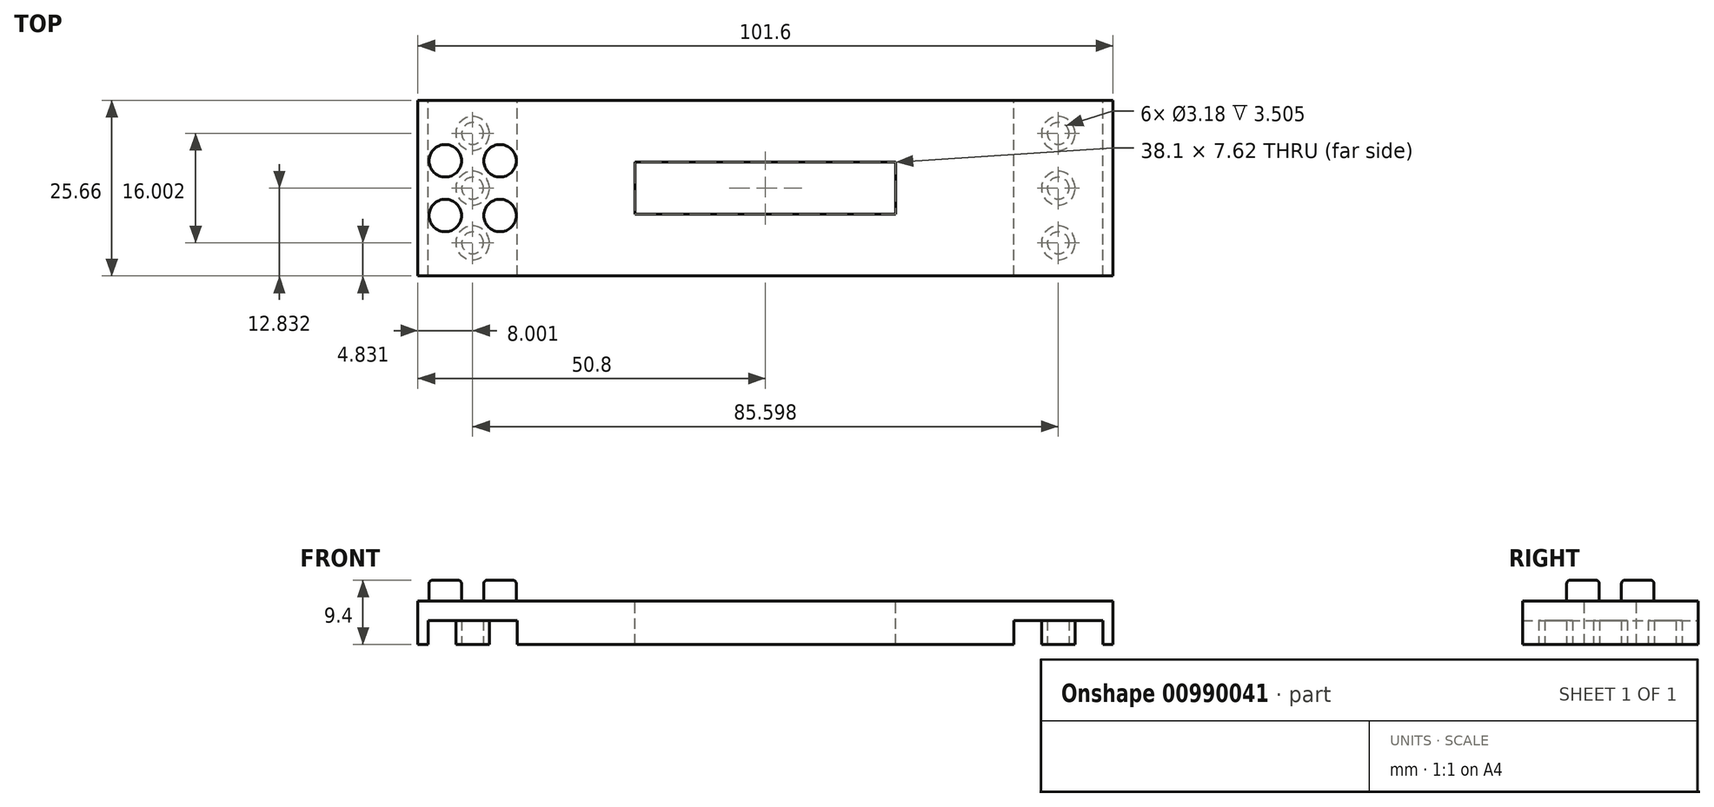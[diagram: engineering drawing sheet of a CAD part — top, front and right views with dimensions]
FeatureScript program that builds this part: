
annotation { "Feature Type Name" : "Feature", "Feature Type Description" : "" }
export const myFeature = defineFeature(function(context is Context, id is Id, definition is map)
    precondition{}
    {
        {
            var Q0;
            Q0=qCreatedBy(makeId("Top.planeOp"),FACE);
            var sketch = newSketch(context, id + "F0", { "sketchPlane" : qUnion([Q0])});
            skLineSegment(sketch, "E0.bottom", {"start": v(0, 0) * mm, "end": v(101.6, 0) * mm});
            skLineSegment(sketch, "E0.top", {"start": v(0, 32) * mm, "end": v(101.6, 32) * mm});
            skLineSegment(sketch, "E0.left", {"start": v(0, 0) * mm, "end": v(0, 32) * mm});
            skLineSegment(sketch, "E0.right", {"start": v(101.6, 0) * mm, "end": v(101.6, 32) * mm});
            skSolve(sketch);
        }
        {
            var Q0;
            Q0=makeQuery(id+"F0.imprint","IMPRINT",FACE,{"disambiguationData":[TD([[makeQuery(id+"F0.imprint","IMPRINT",EDGE,{"derivedFrom":sQuery(id+"F0.wireOp",EDGE,"E0.bottom")}),1.0]])]});
            extrude(context, id + "F1", {"entities" : qUnion([Q0]), "depth" : 6.35 * mm, "offsetDistance" : 25.4 * mm});
        }
        {
            var Q0;
            Q0=makeQuery(id+"F1.opExtrude","CAP_FACE",FACE,{"disambiguationData":[OSD([sQuery(id+"F0.wireOp",EDGE,"E0.bottom"),sQuery(id+"F0.wireOp",EDGE,"E0.top"),sQuery(id+"F0.wireOp",EDGE,"E0.left"),sQuery(id+"F0.wireOp",EDGE,"E0.right")])],"isStart":false});
            var sketch = newSketch(context, id + "F2", { "sketchPlane" : qUnion([Q0])});
            skCircle(sketch, "E1", {"center": v(4, 20) * mm, "radius": 2.37 * mm});
            skCircle(sketch, "E2.0.1.0", {"center": v(4, 12) * mm, "radius": 2.37 * mm});
            skCircle(sketch, "E2.1.0.0", {"center": v(12, 20) * mm, "radius": 2.37 * mm});
            skCircle(sketch, "E2.1.1.0", {"center": v(12, 12) * mm, "radius": 2.37 * mm});
            skLineSegment(sketch, "E2.direction1", {"start": v(4, 20) * mm, "end": v(12, 20) * mm, "construction": true});
            skLineSegment(sketch, "E2.direction2", {"start": v(4, 20) * mm, "end": v(4, 12) * mm, "construction": true});
            skLineSegment(sketch, "E3", {"start": v(4, 20) * mm, "end": v(4, 12) * mm});
            skLineSegment(sketch, "E4", {"start": v(12, 20) * mm, "end": v(12, 12) * mm, "construction": true});
            skLineSegment(sketch, "E5", {"start": v(4, 16) * mm, "end": v(12, 16) * mm, "construction": true});
            skSolve(sketch);
        }
        {
            var Q0;
            Q0=makeQuery(id+"F2.imprint","IMPRINT",FACE,{"disambiguationData":[TD([[makeQuery(id+"F2.imprint","IMPRINT",EDGE,{"derivedFrom":sQuery(id+"F2.wireOp",EDGE,"E2.1.0.0")}),1.0]])]});
            var Q1;
            Q1=makeQuery(id+"F2.imprint","IMPRINT",FACE,{"disambiguationData":[TD([[makeQuery(id+"F2.imprint","IMPRINT",EDGE,{"derivedFrom":sQuery(id+"F2.wireOp",EDGE,"E2.1.1.0")}),1.0]])]});
            var Q2;
            Q2=makeQuery(id+"F2.imprint","IMPRINT",FACE,{"disambiguationData":[TD([[makeQuery(id+"F2.imprint","IMPRINT",EDGE,{"derivedFrom":sQuery(id+"F2.wireOp",EDGE,"E2.0.1.0")}),1.0]])]});
            var Q3;
            Q3=makeQuery(id+"F2.imprint","IMPRINT",FACE,{"disambiguationData":[TD([[makeQuery(id+"F2.imprint","IMPRINT",EDGE,{"derivedFrom":sQuery(id+"F2.wireOp",EDGE,"E1")}),1.0]])]});
            extrude(context, id + "F3", {"entities" : qUnion([Q0, Q1, Q2, Q3]), "operationType" : NewBodyOperationType.ADD, "depth" : 3.05 * mm, "offsetDistance" : 25.4 * mm});
        }
        {
            var Q0;
            Q0=makeQuery(id+"F3.opExtrude","CAP_EDGE",EDGE,{"disambiguationData":[OSD([sQuery(id+"F2.wireOp",EDGE,"E2.1.0.0")])],"isStart":false});
            var Q1;
            Q1=makeQuery(id+"F3.opExtrude","CAP_EDGE",EDGE,{"disambiguationData":[OSD([sQuery(id+"F2.wireOp",EDGE,"E1")])],"isStart":false});
            var Q2;
            Q2=makeQuery(id+"F3.opExtrude","CAP_EDGE",EDGE,{"disambiguationData":[OSD([sQuery(id+"F2.wireOp",EDGE,"E2.0.1.0")])],"isStart":false});
            var Q3;
            Q3=makeQuery(id+"F3.opExtrude","CAP_EDGE",EDGE,{"disambiguationData":[OSD([sQuery(id+"F2.wireOp",EDGE,"E2.1.1.0")])],"isStart":false});
            fillet(context, id + "F4", {"entities" : qUnion([Q0, Q1, Q2, Q3]), "radius" : 0.5 * mm, "tangentPropagation" : true, "allowEdgeOverflow" : false});
        }
        {
            var Q0;
            Q0=makeQuery(id+"F1.opExtrude","CAP_FACE",FACE,{"disambiguationData":[OSD([sQuery(id+"F0.wireOp",EDGE,"E0.bottom"),sQuery(id+"F0.wireOp",EDGE,"E0.top"),sQuery(id+"F0.wireOp",EDGE,"E0.left"),sQuery(id+"F0.wireOp",EDGE,"E0.right")])],"isStart":true});
            var sketch = newSketch(context, id + "F5", { "sketchPlane" : qUnion([Q0])});
            skLineSegment(sketch, "E6.bottom", {"start": v(0, -32) * mm, "end": v(16, -32) * mm, "construction": true});
            skLineSegment(sketch, "E6.top", {"start": v(0, 0) * mm, "end": v(16, 0) * mm, "construction": true});
            skLineSegment(sketch, "E6.left", {"start": v(0, -32) * mm, "end": v(0, 0) * mm, "construction": true});
            skLineSegment(sketch, "E6.right", {"start": v(16, -32) * mm, "end": v(16, 0) * mm, "construction": true});
            skLineSegment(sketch, "E7.bottom", {"start": v(101.6, 0) * mm, "end": v(85.6, 0) * mm, "construction": true});
            skLineSegment(sketch, "E7.top", {"start": v(101.6, -32) * mm, "end": v(85.6, -32) * mm, "construction": true});
            skLineSegment(sketch, "E7.left", {"start": v(101.6, 0) * mm, "end": v(101.6, -32) * mm, "construction": true});
            skLineSegment(sketch, "E7.right", {"start": v(85.6, 0) * mm, "end": v(85.6, -32) * mm, "construction": true});
            skCircle(sketch, "E8", {"center": v(8, -16) * mm, "radius": 2.47 * mm});
            skCircle(sketch, "E9", {"center": v(8, -16) * mm, "radius": 1.59 * mm});
            skCircle(sketch, "E10", {"center": v(8, -8) * mm, "radius": 2.47 * mm});
            skCircle(sketch, "E11", {"center": v(8, -8) * mm, "radius": 1.59 * mm});
            skCircle(sketch, "E12", {"center": v(8, -24) * mm, "radius": 2.47 * mm});
            skCircle(sketch, "E13", {"center": v(8, -24) * mm, "radius": 1.59 * mm});
            skCircle(sketch, "E14", {"center": v(93.6, -16) * mm, "radius": 2.47 * mm});
            skCircle(sketch, "E15", {"center": v(93.6, -16) * mm, "radius": 1.59 * mm});
            skCircle(sketch, "E16", {"center": v(93.6, -8) * mm, "radius": 2.47 * mm});
            skCircle(sketch, "E17", {"center": v(93.6, -8) * mm, "radius": 1.59 * mm});
            skCircle(sketch, "E18", {"center": v(93.6, -24) * mm, "radius": 2.47 * mm});
            skCircle(sketch, "E19", {"center": v(93.6, -24) * mm, "radius": 1.59 * mm});
            skLineSegment(sketch, "E20", {"start": v(0, -16) * mm, "end": v(8, -16) * mm, "construction": true});
            skLineSegment(sketch, "E21", {"start": v(101.6, -16) * mm, "end": v(93.6, -16) * mm, "construction": true});
            skLineSegment(sketch, "E22", {"start": v(8, 0) * mm, "end": v(8, -8) * mm, "construction": true});
            skLineSegment(sketch, "E23", {"start": v(93.6, 0) * mm, "end": v(93.6, -8) * mm, "construction": true});
            skLineSegment(sketch, "E24", {"start": v(8, -8) * mm, "end": v(8, -16) * mm, "construction": true});
            skLineSegment(sketch, "E25", {"start": v(8, -16) * mm, "end": v(8, -24) * mm, "construction": true});
            skLineSegment(sketch, "E26", {"start": v(93.6, -8) * mm, "end": v(93.6, -16) * mm, "construction": true});
            skLineSegment(sketch, "E27", {"start": v(93.6, -16) * mm, "end": v(93.6, -24) * mm, "construction": true});
            skLineSegment(sketch, "E28.bottom", {"start": v(1.5, -1.5) * mm, "end": v(14.5, -1.5) * mm});
            skLineSegment(sketch, "E28.top", {"start": v(1.5, -30.5) * mm, "end": v(14.5, -30.5) * mm});
            skLineSegment(sketch, "E28.left", {"start": v(1.5, -1.5) * mm, "end": v(1.5, -30.5) * mm});
            skLineSegment(sketch, "E28.right", {"start": v(14.5, -1.5) * mm, "end": v(14.5, -30.5) * mm});
            skLineSegment(sketch, "E29.bottom", {"start": v(87.1, -1.5) * mm, "end": v(100.1, -1.5) * mm});
            skLineSegment(sketch, "E29.top", {"start": v(87.1, -30.5) * mm, "end": v(100.1, -30.5) * mm});
            skLineSegment(sketch, "E29.left", {"start": v(87.1, -1.5) * mm, "end": v(87.1, -30.5) * mm});
            skLineSegment(sketch, "E29.right", {"start": v(100.1, -1.5) * mm, "end": v(100.1, -30.5) * mm});
            skSolve(sketch);
        }
        {
            var Q0;
            Q0=makeQuery(id+"F5.imprint","IMPRINT",FACE,{"disambiguationData":[TD([[makeQuery(id+"F5.imprint","IMPRINT",EDGE,{"derivedFrom":sQuery(id+"F5.wireOp",EDGE,"E8")}),-1.0]])]});
            var Q1;
            Q1=makeQuery(id+"F5.imprint","IMPRINT",FACE,{"disambiguationData":[TD([[makeQuery(id+"F5.imprint","IMPRINT",EDGE,{"derivedFrom":sQuery(id+"F5.wireOp",EDGE,"E14")}),-1.0]])]});
            var Q2;
            Q2=makeQuery(id+"F5.imprint","IMPRINT",FACE,{"disambiguationData":[TD([[makeQuery(id+"F5.imprint","IMPRINT",EDGE,{"derivedFrom":sQuery(id+"F5.wireOp",EDGE,"E11")}),1.0]])]});
            var Q3;
            Q3=makeQuery(id+"F5.imprint","IMPRINT",FACE,{"disambiguationData":[TD([[makeQuery(id+"F5.imprint","IMPRINT",EDGE,{"derivedFrom":sQuery(id+"F5.wireOp",EDGE,"E9")}),1.0]])]});
            var Q4;
            Q4=makeQuery(id+"F5.imprint","IMPRINT",FACE,{"disambiguationData":[TD([[makeQuery(id+"F5.imprint","IMPRINT",EDGE,{"derivedFrom":sQuery(id+"F5.wireOp",EDGE,"E13")}),1.0]])]});
            var Q5;
            Q5=makeQuery(id+"F5.imprint","IMPRINT",FACE,{"disambiguationData":[TD([[makeQuery(id+"F5.imprint","IMPRINT",EDGE,{"derivedFrom":sQuery(id+"F5.wireOp",EDGE,"E17")}),1.0]])]});
            var Q6;
            Q6=makeQuery(id+"F5.imprint","IMPRINT",FACE,{"disambiguationData":[TD([[makeQuery(id+"F5.imprint","IMPRINT",EDGE,{"derivedFrom":sQuery(id+"F5.wireOp",EDGE,"E15")}),1.0]])]});
            var Q7;
            Q7=makeQuery(id+"F5.imprint","IMPRINT",FACE,{"disambiguationData":[TD([[makeQuery(id+"F5.imprint","IMPRINT",EDGE,{"derivedFrom":sQuery(id+"F5.wireOp",EDGE,"E19")}),1.0]])]});
            extrude(context, id + "F6", {"entities" : qUnion([Q0, Q1, Q2, Q3, Q4, Q5, Q6, Q7]), "operationType" : NewBodyOperationType.REMOVE, "oppositeDirection" : true, "depth" : 3.5 * mm, "offsetDistance" : 25.4 * mm});
        }
        {
            var Q0;
            {var subQ0=sQuery(id+"F0.wireOp",EDGE,"E0.bottom");var subQ1=sQuery(id+"F0.wireOp",EDGE,"E0.right");var subQ2=sQuery(id+"F0.wireOp",EDGE,"E0.top");var subQ3=sQuery(id+"F0.wireOp",EDGE,"E0.left");Q0=makeQuery(id+"F6.boolean.opBoolean","SPLIT",FACE,{"disambiguationData":[TD([makeQuery(id+"F1.opExtrude","SWEPT_FACE",FACE,{"disambiguationData":[OSD([subQ0])]})])],"derivedFrom":makeQuery(id+"F1.opExtrude","CAP_FACE",FACE,{"disambiguationData":[OSD([subQ0,subQ2,subQ3,subQ1])],"isStart":true})});}
            var sketch = newSketch(context, id + "F7", { "sketchPlane" : qUnion([Q0])});
            skLineSegment(sketch, "E30.bottom", {"start": v(101.6, -32) * mm, "end": v(0, -32) * mm});
            skLineSegment(sketch, "E30.top", {"start": v(101.6, -28.83) * mm, "end": v(0, -28.83) * mm});
            skLineSegment(sketch, "E30.left", {"start": v(101.6, -32) * mm, "end": v(101.6, -28.83) * mm});
            skLineSegment(sketch, "E30.right", {"start": v(0, -32) * mm, "end": v(0, -28.83) * mm});
            skLineSegment(sketch, "E31.bottom", {"start": v(101.6, 0) * mm, "end": v(0, 0) * mm});
            skLineSegment(sketch, "E31.top", {"start": v(101.6, -3.17) * mm, "end": v(0, -3.18) * mm});
            skLineSegment(sketch, "E31.left", {"start": v(101.6, 0) * mm, "end": v(101.6, -3.17) * mm});
            skLineSegment(sketch, "E31.right", {"start": v(0, 0) * mm, "end": v(0, -3.18) * mm});
            skSolve(sketch);
        }
        {
            var Q0;
            Q0=qSketchRegion(id+"F7",true);
            extrude(context, id + "F8", {"entities" : qUnion([Q0]), "operationType" : NewBodyOperationType.REMOVE, "endBound" : BoundingType.UP_TO_NEXT, "oppositeDirection" : true, "depth" : 25.4 * mm, "offsetDistance" : 25.4 * mm});
        }
        {
            var Q0;
            Q0=makeQuery(id+"F1.opExtrude","CAP_FACE",FACE,{"disambiguationData":[OSD([sQuery(id+"F0.wireOp",EDGE,"E0.bottom"),sQuery(id+"F0.wireOp",EDGE,"E0.top"),sQuery(id+"F0.wireOp",EDGE,"E0.left"),sQuery(id+"F0.wireOp",EDGE,"E0.right")])],"isStart":false});
            var sketch = newSketch(context, id + "F9", { "sketchPlane" : qUnion([Q0])});
            skLineSegment(sketch, "E32.bottom", {"start": v(69.85, 12.2) * mm, "end": v(31.75, 12.2) * mm});
            skLineSegment(sketch, "E32.top", {"start": v(69.85, 19.81) * mm, "end": v(31.75, 19.81) * mm});
            skLineSegment(sketch, "E32.left", {"start": v(69.85, 12.2) * mm, "end": v(69.85, 19.81) * mm});
            skLineSegment(sketch, "E32.right", {"start": v(31.75, 12.2) * mm, "end": v(31.75, 19.81) * mm});
            skLineSegment(sketch, "E33", {"start": v(69.85, 16) * mm, "end": v(101.6, 16) * mm, "construction": true});
            skLineSegment(sketch, "E34", {"start": v(50.8, 12.2) * mm, "end": v(50.8, 3.18) * mm, "construction": true});
            skSolve(sketch);
        }
        {
            var Q0;
            Q0=qSketchRegion(id+"F9",true);
            extrude(context, id + "F10", {"entities" : qUnion([Q0]), "operationType" : NewBodyOperationType.REMOVE, "endBound" : BoundingType.UP_TO_NEXT, "oppositeDirection" : true, "depth" : 25.4 * mm, "offsetDistance" : 25.4 * mm});
        }
    });
